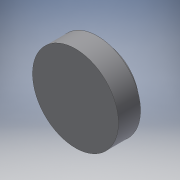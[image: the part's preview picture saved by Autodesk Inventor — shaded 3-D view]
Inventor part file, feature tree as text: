
AUTODESK INVENTOR PART (.ipt)
format: ipt  version: 2016 SP2 (Build 200236200, 236)  size: 99,328 bytes
history: native  units: mm
features: extrude x2, sketch x2
ambient origin geometry x8: Origin, YZ Plane, XZ Plane, XY Plane, X Axis, Y Axis, Z Axis, Center Point
bodies: Volumenkörper1 (feature_tree)
feature tree (4):
  extrude  "Extrusion1"  Depth=3.8mm TaperAngle=0.0deg
  extrude  "Extrusion2"  Depth=1.2mm TaperAngle=0.0deg
  sketch  "Skizze1"  dims[d0=14.8mm d1=3.8mm d2=0.0mm]
  sketch  "Skizze2"  dims[d3=11.8mm d4=1.2mm d5=0.0mm]
